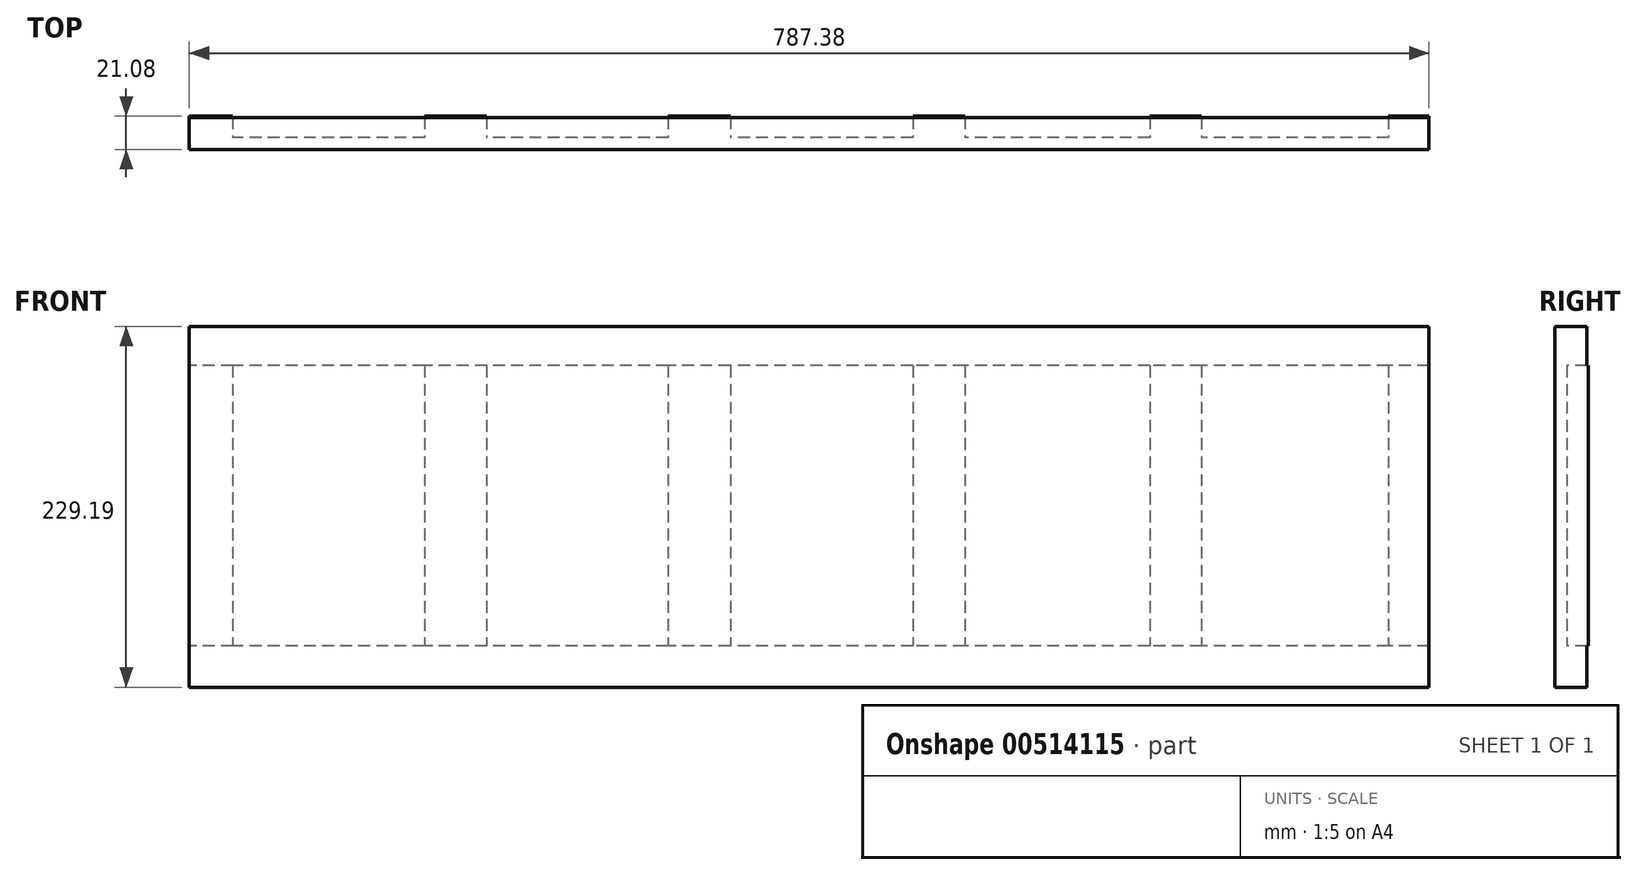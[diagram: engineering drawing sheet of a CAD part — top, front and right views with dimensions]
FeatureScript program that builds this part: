
annotation { "Feature Type Name" : "Feature", "Feature Type Description" : "" }
export const myFeature = defineFeature(function(context is Context, id is Id, definition is map)
    precondition{}
    {
        {
            var Q0;
            Q0=qCreatedBy(makeId("Front.planeOp"),FACE);
            var sketch = newSketch(context, id + "F0", { "sketchPlane" : qUnion([Q0])});
            skLineSegment(sketch, "E0.bottom", {"start": v(-350.5, 116.15) * mm, "end": v(436.88, 116.15) * mm});
            skLineSegment(sketch, "E0.top", {"start": v(-350.5, -113.04) * mm, "end": v(436.88, -113.04) * mm});
            skLineSegment(sketch, "E0.left", {"start": v(-350.5, 116.15) * mm, "end": v(-350.5, -113.04) * mm});
            skLineSegment(sketch, "E0.right", {"start": v(436.88, 116.15) * mm, "end": v(436.88, -113.04) * mm});
            skSolve(sketch);
        }
        {
            var Q0;
            Q0=makeQuery(id+"F0.imprint","IMPRINT",FACE,{"disambiguationData":[TD([[makeQuery(id+"F0.imprint","IMPRINT",EDGE,{"derivedFrom":sQuery(id+"F0.wireOp",EDGE,"E0.bottom")}),-1.0]])]});
            extrude(context, id + "F1", {"entities" : qUnion([Q0]), "depth" : 7.62 * mm});
        }
        {
            var Q0;
            Q0=makeQuery(id+"F1.opExtrude","CAP_FACE",FACE,{"disambiguationData":[OSD([sQuery(id+"F0.wireOp",EDGE,"E0.bottom"),sQuery(id+"F0.wireOp",EDGE,"E0.top"),sQuery(id+"F0.wireOp",EDGE,"E0.left"),sQuery(id+"F0.wireOp",EDGE,"E0.right")])],"isStart":true});
            var sketch = newSketch(context, id + "F2", { "sketchPlane" : qUnion([Q0])});
            skLineSegment(sketch, "E1.bottom", {"start": v(-436.88, 116.15) * mm, "end": v(350.5, 116.15) * mm});
            skLineSegment(sketch, "E1.top", {"start": v(-436.88, 91.25) * mm, "end": v(350.5, 91.25) * mm});
            skLineSegment(sketch, "E1.left", {"start": v(-436.88, 116.15) * mm, "end": v(-436.88, 91.25) * mm});
            skLineSegment(sketch, "E1.right", {"start": v(350.5, 116.15) * mm, "end": v(350.5, 91.25) * mm});
            skSolve(sketch);
        }
        {
            var Q0;
            Q0=makeQuery(id+"F2.imprint","IMPRINT",FACE,{"disambiguationData":[TD([[makeQuery(id+"F2.imprint","IMPRINT",EDGE,{"derivedFrom":sQuery(id+"F2.wireOp",EDGE,"E1.bottom")}),1.0]])]});
            extrude(context, id + "F3", {"entities" : qUnion([Q0]), "operationType" : NewBodyOperationType.ADD, "depth" : 12.7 * mm});
        }
        {
            var Q0;
            Q0=makeQuery(id+"F1.opExtrude","CAP_FACE",FACE,{"disambiguationData":[OSD([sQuery(id+"F0.wireOp",EDGE,"E0.bottom"),sQuery(id+"F0.wireOp",EDGE,"E0.top"),sQuery(id+"F0.wireOp",EDGE,"E0.left"),sQuery(id+"F0.wireOp",EDGE,"E0.right")])],"isStart":true});
            var sketch = newSketch(context, id + "F4", { "sketchPlane" : qUnion([Q0])});
            skLineSegment(sketch, "E2.bottom", {"start": v(-436.88, -113.04) * mm, "end": v(350.5, -113.04) * mm});
            skLineSegment(sketch, "E2.top", {"start": v(-436.88, -86.77) * mm, "end": v(350.5, -86.77) * mm});
            skLineSegment(sketch, "E2.left", {"start": v(-436.88, -113.04) * mm, "end": v(-436.88, -86.77) * mm});
            skLineSegment(sketch, "E2.right", {"start": v(350.5, -113.04) * mm, "end": v(350.5, -86.77) * mm});
            skSolve(sketch);
        }
        {
            var Q0;
            Q0 = qSketchRegion(id + "F4", true);
            extrude(context, id + "F5", {"entities" : qUnion([Q0]), "operationType" : NewBodyOperationType.ADD, "depth" : 12.7 * mm});
        }
        {
            var Q0;
            Q0=makeQuery(id+"F1.opExtrude","CAP_FACE",FACE,{"disambiguationData":[OSD([sQuery(id+"F0.wireOp",EDGE,"E0.bottom"),sQuery(id+"F0.wireOp",EDGE,"E0.top"),sQuery(id+"F0.wireOp",EDGE,"E0.left"),sQuery(id+"F0.wireOp",EDGE,"E0.right")])],"isStart":true});
            var sketch = newSketch(context, id + "F6", { "sketchPlane" : qUnion([Q0])});
            skLineSegment(sketch, "E3.bottom", {"start": v(-436.88, 91.25) * mm, "end": v(-411.16, 91.25) * mm});
            skLineSegment(sketch, "E3.top", {"start": v(-436.88, -86.77) * mm, "end": v(-411.16, -86.77) * mm});
            skLineSegment(sketch, "E3.left", {"start": v(-436.88, 91.25) * mm, "end": v(-436.88, -86.77) * mm});
            skLineSegment(sketch, "E3.right", {"start": v(-411.16, 91.25) * mm, "end": v(-411.16, -86.77) * mm});
            skSolve(sketch);
        }
        {
            var Q0;
            Q0 = qSketchRegion(id + "F6", true);
            extrude(context, id + "F7", {"entities" : qUnion([Q0]), "operationType" : NewBodyOperationType.ADD, "depth" : 13.46 * mm});
        }
        {
            var Q0;
            Q0=makeQuery(id+"F1.opExtrude","CAP_FACE",FACE,{"disambiguationData":[OSD([sQuery(id+"F0.wireOp",EDGE,"E0.bottom"),sQuery(id+"F0.wireOp",EDGE,"E0.top"),sQuery(id+"F0.wireOp",EDGE,"E0.left"),sQuery(id+"F0.wireOp",EDGE,"E0.right")])],"isStart":true});
            var sketch = newSketch(context, id + "F8", { "sketchPlane" : qUnion([Q0])});
            skLineSegment(sketch, "E4.bottom", {"start": v(350.5, 91.25) * mm, "end": v(322.91, 91.25) * mm});
            skLineSegment(sketch, "E4.top", {"start": v(350.5, -86.77) * mm, "end": v(322.91, -86.77) * mm});
            skLineSegment(sketch, "E4.left", {"start": v(350.5, 91.25) * mm, "end": v(350.5, -86.77) * mm});
            skLineSegment(sketch, "E4.right", {"start": v(322.91, 91.25) * mm, "end": v(322.91, -86.77) * mm});
            skSolve(sketch);
        }
        {
            var Q0;
            Q0=makeQuery(id+"F8.imprint","IMPRINT",FACE,{"disambiguationData":[TD([[makeQuery(id+"F8.imprint","IMPRINT",EDGE,{"derivedFrom":sQuery(id+"F8.wireOp",EDGE,"E4.bottom")}),-1.0]])]});
            extrude(context, id + "F9", {"entities" : qUnion([Q0]), "operationType" : NewBodyOperationType.ADD, "depth" : 13.46 * mm});
        }
        {
            var Q0;
            Q0=makeQuery(id+"F1.opExtrude","CAP_FACE",FACE,{"disambiguationData":[OSD([sQuery(id+"F0.wireOp",EDGE,"E0.bottom"),sQuery(id+"F0.wireOp",EDGE,"E0.top"),sQuery(id+"F0.wireOp",EDGE,"E0.left"),sQuery(id+"F0.wireOp",EDGE,"E0.right")])],"isStart":true});
            var sketch = newSketch(context, id + "F10", { "sketchPlane" : qUnion([Q0])});
            skLineSegment(sketch, "E5.bottom", {"start": v(-292.46, 91.25) * mm, "end": v(-259.5, 91.25) * mm});
            skLineSegment(sketch, "E5.top", {"start": v(-292.46, -86.77) * mm, "end": v(-259.5, -86.77) * mm});
            skLineSegment(sketch, "E5.left", {"start": v(-292.46, 91.25) * mm, "end": v(-292.46, -86.77) * mm});
            skLineSegment(sketch, "E5.right", {"start": v(-259.5, 91.25) * mm, "end": v(-259.5, -86.77) * mm});
            skSolve(sketch);
        }
        {
            var Q0;
            Q0=makeQuery(id+"F10.imprint","IMPRINT",FACE,{"disambiguationData":[TD([[makeQuery(id+"F10.imprint","IMPRINT",EDGE,{"derivedFrom":sQuery(id+"F10.wireOp",EDGE,"E5.bottom")}),-1.0]])]});
            extrude(context, id + "F11", {"entities" : qUnion([Q0]), "operationType" : NewBodyOperationType.ADD, "depth" : 13.46 * mm});
        }
        {
            var Q0;
            Q0=makeQuery(id+"F11.boolean.opBoolean","SPLIT",FACE,{"disambiguationData":[TD([makeQuery(id+"F9.opExtrude","SWEPT_FACE",FACE,{"disambiguationData":[OSD([sQuery(id+"F8.wireOp",EDGE,"E4.right")])]})])],"derivedFrom":makeQuery(id+"F1.opExtrude","CAP_FACE",FACE,{"disambiguationData":[OSD([sQuery(id+"F0.wireOp",EDGE,"E0.bottom"),sQuery(id+"F0.wireOp",EDGE,"E0.top"),sQuery(id+"F0.wireOp",EDGE,"E0.left"),sQuery(id+"F0.wireOp",EDGE,"E0.right")])],"isStart":true})});
            var sketch = newSketch(context, id + "F12", { "sketchPlane" : qUnion([Q0])});
            skLineSegment(sketch, "E6.bottom", {"start": v(-142, 91.25) * mm, "end": v(-109.03, 91.25) * mm});
            skLineSegment(sketch, "E6.top", {"start": v(-142, -86.77) * mm, "end": v(-109.03, -86.77) * mm});
            skLineSegment(sketch, "E6.left", {"start": v(-142, 91.25) * mm, "end": v(-142, -86.77) * mm});
            skLineSegment(sketch, "E6.right", {"start": v(-109.03, 91.25) * mm, "end": v(-109.03, -86.77) * mm});
            skSolve(sketch);
        }
        {
            var Q0;
            Q0=makeQuery(id+"F12.imprint","IMPRINT",FACE,{"disambiguationData":[TD([[makeQuery(id+"F12.imprint","IMPRINT",EDGE,{"derivedFrom":sQuery(id+"F12.wireOp",EDGE,"E6.bottom")}),-1.0]])]});
            extrude(context, id + "F13", {"entities" : qUnion([Q0]), "operationType" : NewBodyOperationType.ADD, "depth" : 13.46 * mm});
        }
        {
            var Q0;
            {var subQ2=makeQuery(id+"F9.opExtrude","SWEPT_FACE",FACE,{"disambiguationData":[OSD([sQuery(id+"F8.wireOp",EDGE,"E4.right")])]});Q0=makeQuery(id+"F13.boolean.opBoolean","SPLIT",FACE,{"disambiguationData":[TD([subQ2])],"derivedFrom":makeQuery(id+"F11.boolean.opBoolean","SPLIT",FACE,{"disambiguationData":[TD([subQ2])],"derivedFrom":makeQuery(id+"F1.opExtrude","CAP_FACE",FACE,{"disambiguationData":[OSD([sQuery(id+"F0.wireOp",EDGE,"E0.bottom"),sQuery(id+"F0.wireOp",EDGE,"E0.top"),sQuery(id+"F0.wireOp",EDGE,"E0.left"),sQuery(id+"F0.wireOp",EDGE,"E0.right")])],"isStart":true})})});}
            var sketch = newSketch(context, id + "F14", { "sketchPlane" : qUnion([Q0])});
            skLineSegment(sketch, "E7.bottom", {"start": v(6.9, 91.25) * mm, "end": v(46.46, 91.25) * mm});
            skLineSegment(sketch, "E7.top", {"start": v(6.9, -86.77) * mm, "end": v(46.46, -86.77) * mm});
            skLineSegment(sketch, "E7.left", {"start": v(6.9, 91.25) * mm, "end": v(6.9, -86.77) * mm});
            skLineSegment(sketch, "E7.right", {"start": v(46.46, 91.25) * mm, "end": v(46.46, -86.77) * mm});
            skSolve(sketch);
        }
        {
            var Q0;
            Q0=makeQuery(id+"F14.imprint","IMPRINT",FACE,{"disambiguationData":[TD([[makeQuery(id+"F14.imprint","IMPRINT",EDGE,{"derivedFrom":sQuery(id+"F14.wireOp",EDGE,"E7.bottom")}),-1.0]])]});
            extrude(context, id + "F15", {"entities" : qUnion([Q0]), "operationType" : NewBodyOperationType.ADD, "depth" : 13.46 * mm});
        }
        {
            var Q0;
            {var subQ2=makeQuery(id+"F9.opExtrude","SWEPT_FACE",FACE,{"disambiguationData":[OSD([sQuery(id+"F8.wireOp",EDGE,"E4.right")])]});Q0=makeQuery(id+"F15.boolean.opBoolean","SPLIT",FACE,{"disambiguationData":[TD([subQ2])],"derivedFrom":makeQuery(id+"F13.boolean.opBoolean","SPLIT",FACE,{"disambiguationData":[TD([subQ2])],"derivedFrom":makeQuery(id+"F11.boolean.opBoolean","SPLIT",FACE,{"disambiguationData":[TD([subQ2])],"derivedFrom":makeQuery(id+"F1.opExtrude","CAP_FACE",FACE,{"disambiguationData":[OSD([sQuery(id+"F0.wireOp",EDGE,"E0.bottom"),sQuery(id+"F0.wireOp",EDGE,"E0.top"),sQuery(id+"F0.wireOp",EDGE,"E0.left"),sQuery(id+"F0.wireOp",EDGE,"E0.right")])],"isStart":true})})})});}
            var sketch = newSketch(context, id + "F16", { "sketchPlane" : qUnion([Q0])});
            skLineSegment(sketch, "E8.bottom", {"start": v(161.6, 91.25) * mm, "end": v(201.17, 91.25) * mm});
            skLineSegment(sketch, "E8.top", {"start": v(161.6, -86.77) * mm, "end": v(201.17, -86.77) * mm});
            skLineSegment(sketch, "E8.left", {"start": v(161.6, 91.25) * mm, "end": v(161.6, -86.77) * mm});
            skLineSegment(sketch, "E8.right", {"start": v(201.17, 91.25) * mm, "end": v(201.17, -86.77) * mm});
            skSolve(sketch);
        }
        {
            var Q0;
            Q0=makeQuery(id+"F16.imprint","IMPRINT",FACE,{"disambiguationData":[TD([[makeQuery(id+"F16.imprint","IMPRINT",EDGE,{"derivedFrom":sQuery(id+"F16.wireOp",EDGE,"E8.bottom")}),-1.0]])]});
            extrude(context, id + "F17", {"entities" : qUnion([Q0]), "operationType" : NewBodyOperationType.ADD, "depth" : 13.46 * mm});
        }
    });
